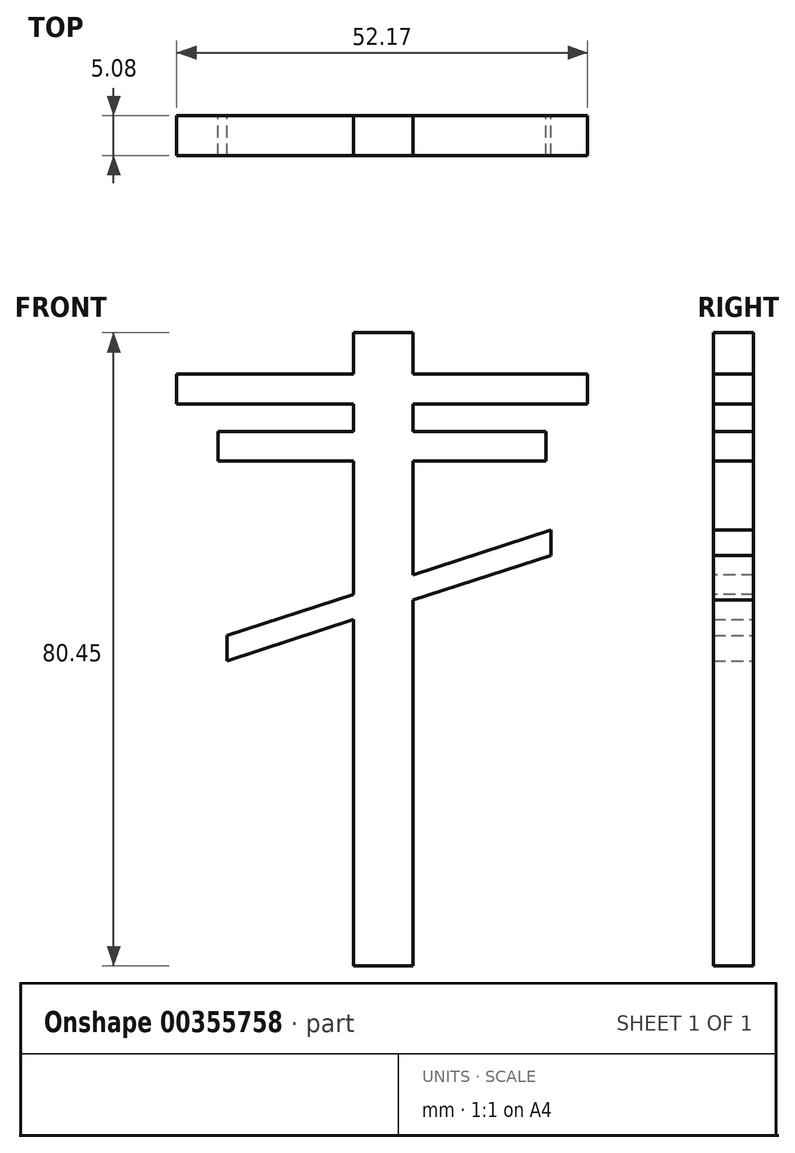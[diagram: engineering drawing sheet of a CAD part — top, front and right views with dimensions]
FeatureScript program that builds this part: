
annotation { "Feature Type Name" : "Feature", "Feature Type Description" : "" }
export const myFeature = defineFeature(function(context is Context, id is Id, definition is map)
    precondition{}
    {
        {
            var Q0;
            Q0=qCreatedBy(makeId("Front.planeOp"),FACE);
            var sketch = newSketch(context, id + "F0", { "sketchPlane" : qUnion([Q0])});
            skLineSegment(sketch, "E0.bottom", {"start": v(-4.08, 44.16) * mm, "end": v(3.5, 44.16) * mm});
            skLineSegment(sketch, "E0.top", {"start": v(-4.08, -36.29) * mm, "end": v(3.5, -36.29) * mm});
            skLineSegment(sketch, "E0.left", {"start": v(-4.08, 44.16) * mm, "end": v(-4.08, -36.29) * mm});
            skLineSegment(sketch, "E0.right", {"start": v(3.5, 44.16) * mm, "end": v(3.5, -36.29) * mm});
            skSolve(sketch);
        }
        {
            var Q0;
            Q0 = qSketchRegion(id + "F0", true);
            extrude(context, id + "F1", {"entities" : qUnion([Q0]), "depth" : 5.08 * mm});
        }
        {
            var Q0;
            Q0=qCreatedBy(makeId("Front.planeOp"),FACE);
            var sketch = newSketch(context, id + "F2", { "sketchPlane" : qUnion([Q0])});
            skLineSegment(sketch, "E1.bottom", {"start": v(-26.52, 38.91) * mm, "end": v(25.65, 38.91) * mm});
            skLineSegment(sketch, "E1.top", {"start": v(-26.52, 35.12) * mm, "end": v(25.65, 35.12) * mm});
            skLineSegment(sketch, "E1.left", {"start": v(-26.52, 38.91) * mm, "end": v(-26.52, 35.12) * mm});
            skLineSegment(sketch, "E1.right", {"start": v(25.65, 38.91) * mm, "end": v(25.65, 35.12) * mm});
            skLineSegment(sketch, "E2.bottom", {"start": v(-21.28, 31.63) * mm, "end": v(20.4, 31.63) * mm});
            skLineSegment(sketch, "E2.top", {"start": v(-21.28, 27.84) * mm, "end": v(20.4, 27.84) * mm});
            skLineSegment(sketch, "E2.left", {"start": v(-21.28, 31.63) * mm, "end": v(-21.28, 27.84) * mm});
            skLineSegment(sketch, "E2.right", {"start": v(20.4, 31.63) * mm, "end": v(20.4, 27.84) * mm});
            skSolve(sketch);
        }
        {
            var Q0;
            Q0 = qSketchRegion(id + "F2", true);
            extrude(context, id + "F3", {"entities" : qUnion([Q0]), "operationType" : NewBodyOperationType.ADD, "depth" : 5.08 * mm});
        }
        {
            var Q0;
            Q0 = qSketchRegion(id + "F2", true);
            extrude(context, id + "F4", {"entities" : qUnion([Q0]), "operationType" : NewBodyOperationType.ADD, "depth" : 5.08 * mm});
        }
        {
            var Q0;
            Q0=qCreatedBy(makeId("Front.planeOp"),FACE);
            var sketch = newSketch(context, id + "F5", { "sketchPlane" : qUnion([Q0])});
            skLineSegment(sketch, "E3", {"start": v(-20.11, 5.68) * mm, "end": v(20.99, 19.1) * mm});
            skLineSegment(sketch, "E4", {"start": v(20.99, 15.89) * mm, "end": v(-20.11, 2.48) * mm});
            skLineSegment(sketch, "E5", {"start": v(-20.11, 2.48) * mm, "end": v(-20.11, 5.68) * mm});
            skLineSegment(sketch, "E6", {"start": v(20.99, 19.1) * mm, "end": v(20.99, 15.89) * mm});
            skSolve(sketch);
        }
        {
            var Q0;
            Q0 = qSketchRegion(id + "F5", true);
            extrude(context, id + "F6", {"entities" : qUnion([Q0]), "operationType" : NewBodyOperationType.ADD, "depth" : 5.08 * mm});
        }
    });
